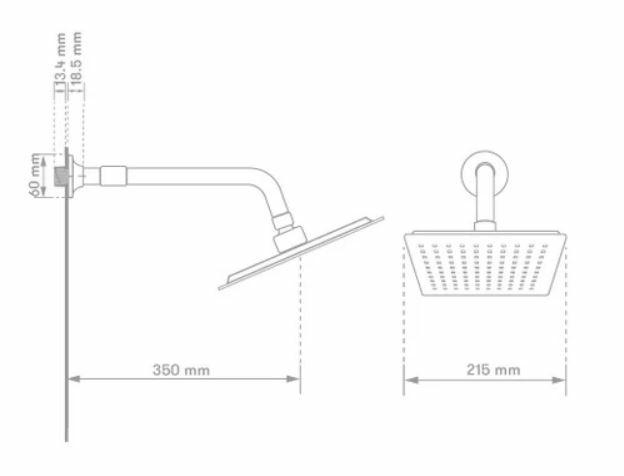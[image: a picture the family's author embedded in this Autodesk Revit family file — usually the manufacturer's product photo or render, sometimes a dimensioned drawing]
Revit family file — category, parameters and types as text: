
# Revit family: BL-2430-11-REGADERA HELVETIA CINCO FUNCIONES
name_source: partatom
category: Plumbing Fixtures
revit_build: Autodesk Revit 2018 (Build: 20170223_1515(x64)
units: mm (PartAtom-declared; Revit-internal decimal feet)

## family parameters
Cut with Voids When Loaded = No
Host = Face
OmniClass Number = 23.31.11.00
Part Type = Normal
Room Calculation Point = No
Round Connector Dimension = Use Diameter
Shared = No

## types (1)
- BL-2430-11
    Alto = 100 mm  [stored 0.328084 ft]
    Ancho = 105 mm  [stored 0.344488 ft]
    CW Connection = Yes
    Default Elevation = 0 mm  [stored 0 ft]
    Description = Regadera
    HW Connection = Yes
    Link Ficha Tecnica = http://infotecnica.gricol.com
    Manufacturer = Gricol
    Model = BL-2430-11
    Plastico ABS Cromado = Plastico ABS Cromado
    Presion Maxima = 125.00 psi
    Product Name = REGADERA HELVETIA CINCO FUNCIONES
    Profundidad = 210 mm  [stored 0.688976 ft]
    Type Image = HELVETIA.JPG
    URL = https://www.gricol.com
    Vent Connection = No
    Waste Connection = No

note: [stored X ft] marks values corroborated as IEEE doubles in the binary element streams (Revit-internal decimal feet)

## geometry (parser evidence)
native form markers: Blend x8, Sweep x16
no freeform markers — native parametric forms only
